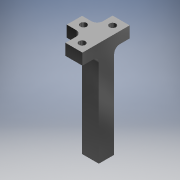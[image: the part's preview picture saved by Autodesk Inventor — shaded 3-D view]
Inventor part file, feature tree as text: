
AUTODESK INVENTOR PART (.ipt)
format: ipt  version: 2018 (Build 220112000, 112)  size: 178,176 bytes
history: native  units: mm
features: sketch x5, other x3
ambient origin geometry x8: Origin, YZ Plane, XZ Plane, XY Plane, X Axis, Y Axis, Z Axis, Center Point
bodies: Volumenkörper1 (feature_tree)
feature tree (8):
  other  "SolarpanelHalterung1.ipt"
  other  "Volumenkörper1::SolarpanelHalterung1.ipt"
  other  "Bezeichnung1"
  sketch  "Skizze1"  dims[d0=10.0mm]
  sketch  "Skizze2"
  sketch  "Skizze3"
  sketch  "Skizze4"
  sketch  "Skizze5"
